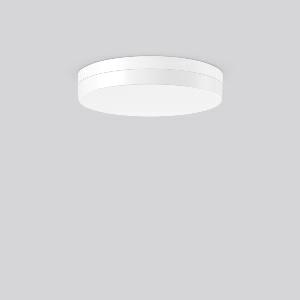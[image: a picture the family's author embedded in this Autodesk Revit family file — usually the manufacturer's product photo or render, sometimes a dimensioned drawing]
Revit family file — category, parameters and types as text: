
# Revit family: flat_slim_round_312632_002_01c9
name_source: partatom
category: Lighting Fixtures
units: mm (PartAtom-declared; Revit-internal decimal feet)

## family parameters
Cut with Voids When Loaded = No
Host = Face
Light Source = No
Part Type = Normal
Room Calculation Point = No
Round Connector Dimension = Use Diameter
Shared = No

## types (1)
- MultiLumen 1 830 (1 x LED Modul 830, 2400 lm, 3000)
    Apparent Load = 20 VA
    CIE Flux Codes = 39 70 90 83 100
    Color Rendering = 80
    Color Temperature = 3000
    Default Elevation = 1800 mm
    Height = 70 mm
    Lamp = 1 x LED Modul 830
    Lamp Light Flux = 2400 lm
    Lamp count = 1
    Length = 400 mm
    Lifetime = 50000 h
    Luminous efficacy = 120 lm/W
    Manufacturer = RZB
    ModVariant = No
    Model = 312632.002
    Mounting Place = Ceiling
    Mounting Type = Surface mounted
    Number of Poles = 1
    OnlyDefault = Yes
    Power Factor = 1
    Product Name = FLAT SLIM round
    Product group = Surface mounted ceiling and wall luminaires
    ProductGroupID = 305
    Protection Class = Protection class I
    Protection Degree = Degree of protection
    RLX_Detail_Level = 1
    RLX_Emergency_Light_Flux = 0 lm
    RLX_Emergency_Type = 0
    RLX_Emergency_Type_DB = No
    RlxData = <blob elided: 19889 chars, md5=dc8a1f96>
    Socket = socket
    Standby Power = 0 W
    System Light Flux = 2400 lm
    System Power = 20 W
    Type Comments = MultiLumen 1 830
    Type Image = 312631.002.jpg
    URL = http://relux.com
    VarID = multilumen_1_830
    Voltage = 0 V
    Weight = 0.00 kg
    Width = 0 mm  [stored 0 ft]

note: [stored X ft] marks values corroborated as IEEE doubles in the binary element streams (Revit-internal decimal feet)

## geometry (parser evidence)
native form markers: Blend x4, Sweep x13
no freeform markers — native parametric forms only
